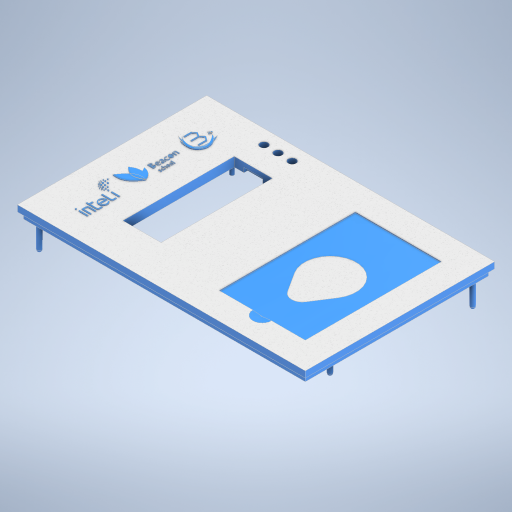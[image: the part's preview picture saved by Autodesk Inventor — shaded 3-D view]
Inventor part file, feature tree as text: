
AUTODESK INVENTOR PART (.ipt)
format: ipt  version: 2023 (Build 270158000, 158)  size: 1,780,736 bytes
history: native  units: mm
features: extrude x26, sketch x19, other x1, fillet x1
ambient origin geometry x8: Origin, YZ Plane, XZ Plane, XY Plane, X Axis, Y Axis, Z Axis, Center Point
bodies: Body1 (feature_tree)
feature tree (47):
  other  "Sólido1"
  sketch  "Esboço1"  dims[d0=184.0mm d1=121.0mm]
  extrude  "Extrusão1"  Depth=121.0mm
  extrude  "Extrusão2"  Depth=87.0mm
  extrude  "Extrusão3"  Depth=13.0mm
  extrude  "Extrusão4"  Depth=71.15mm
  extrude  "Extrusão5"  Depth=8.0mm TaperAngle=0.0deg
  extrude  "Extrusão6"  Depth=0.7mm TaperAngle=0.0deg
  extrude  "Extrusão7"  Depth=12.0mm
  extrude  "Extrusão8"  Depth=0.5mm TaperAngle=0.0deg
  extrude  "Extrusão9"  Depth=0.5mm TaperAngle=0.0deg
  sketch  "Esboço2"  dims[d2=55.0mm d3=87.0mm]
  extrude  "Extrusão10"  Depth=36.05mm
  extrude  "Extrusão11"  Depth=4.0mm
  extrude  "Extrusão12"  Depth=40.0mm
  extrude  "Extrusão13"  Depth=6.0mm
  extrude  "Extrusão14"  Depth=5.0mm TaperAngle=0.0deg
  sketch  "Esboço11"  dims[d19=42.55mm d24=8.0mm d25=0.0mm]
  extrude  "Extrusão15"  Depth=7.0mm TaperAngle=0.0deg
  extrude  "Extrusão16"  Depth=4.0mm TaperAngle=0.0deg
  extrude  "Extrusão17"  Depth=19.0mm
  extrude  "Extrusão18"  Depth=8.0mm
  sketch  "Esboço14"  dims[d30=12.0mm d31=0.6mm d32=-14.660766mm]
  sketch  "Esboço15"  dims[d33=0.5mm d34=0.0mm d35=0.5mm d36=0.0mm]
  sketch  "Esboço16"  dims[d37=0.7mm d38=0.0mm d39=0.5mm d40=0.0mm]
  sketch  "Esboço17"  dims[d41=0.3mm d42=0.0mm d43=36.05mm]
  extrude  "Extrusão19"  Depth=3.0mm TaperAngle=0.0deg
  extrude  "Extrusão20"  Depth=164.0mm
  sketch  "Esboço20"  dims[d49=6.0mm d50=0.0mm d51=6.0mm]
  extrude  "Extrusão21"  Depth=5.0mm TaperAngle=0.0deg
  sketch  "Esboço22"  dims[d55=2.0mm d56=0.0mm d69=7.0mm d70=0.0mm]
  extrude  "Extrusão22"  Depth=39.4mm
  extrude  "Extrusão23"  Depth=60.0mm
  sketch  "Esboço23"  dims[d71=2.0mm d72=4.0mm d73=0.0mm]
  extrude  "Extrusão24"  Depth=6.0mm TaperAngle=0.0deg
  extrude  "Extrusão25"  Depth=20.4mm
  extrude  "Extrusão26"  Depth=0.5mm
  fillet  "Arredondamento1"  Radius=3.0mm
  sketch  "Esboço3"  dims[d5=17.0mm d8=13.0mm]
  sketch  "Esboço4"  dims[d9=24.36mm d10=71.15mm]
  sketch  "Esboço12"  dims[d26=0.6mm d27=0.0mm d28=0.7mm d29=0.0mm]
  sketch  "Esboço18"  dims[d44=79.9mm d45=4.0mm]
  sketch  "Esboço19"  dims[d47=40.0mm d48=6.2mm]
  sketch  "Esboço21"  dims[d52=6.0mm d53=5.0mm d54=0.0mm]
  sketch  "Esboço24"  dims[d106=57.0mm d111=19.0mm]
  sketch  "Esboço25"  dims[d112=28.0mm d113=8.0mm]
  sketch  "Esboço26"  dims[d114=5.0mm d115=0.0mm d116=3.0mm d117=0.0mm d120=164.0mm d122=5.0mm d123=0.0mm d130=39.4mm d131=60.0mm d132=6.0mm d133=0.0mm d136=20.4mm d137=23.4mm d138=3.0mm d139=0.0mm d140=5.0mm d141=5.0mm d142=5.0mm d143=9.0mm d145=9.0mm d149=18.0mm d151=11.469816mm d152=0.0mm d153=0.0mm d158=2.0mm d159=0.0mm d162=2.0mm d163=0.0mm d166=10.0mm d167=2.8mm d168=2.0mm d169=0.0mm d170=15.700077mm d171=2.0mm d172=0.0mm d173=2.0mm d174=0.0mm d177=3.0mm d180=3.0mm d183=3.0mm d184=3.0mm d185=18.0mm d186=0.0mm d191=1.5mm d57=0.5mm d58=0.872665mm d59=0.5mm d60=0.872665mm d86=0.872665mm d87=0.872665mm d124=0.5mm d125=0.872665mm d175=0.5mm d176=0.872665mm]
